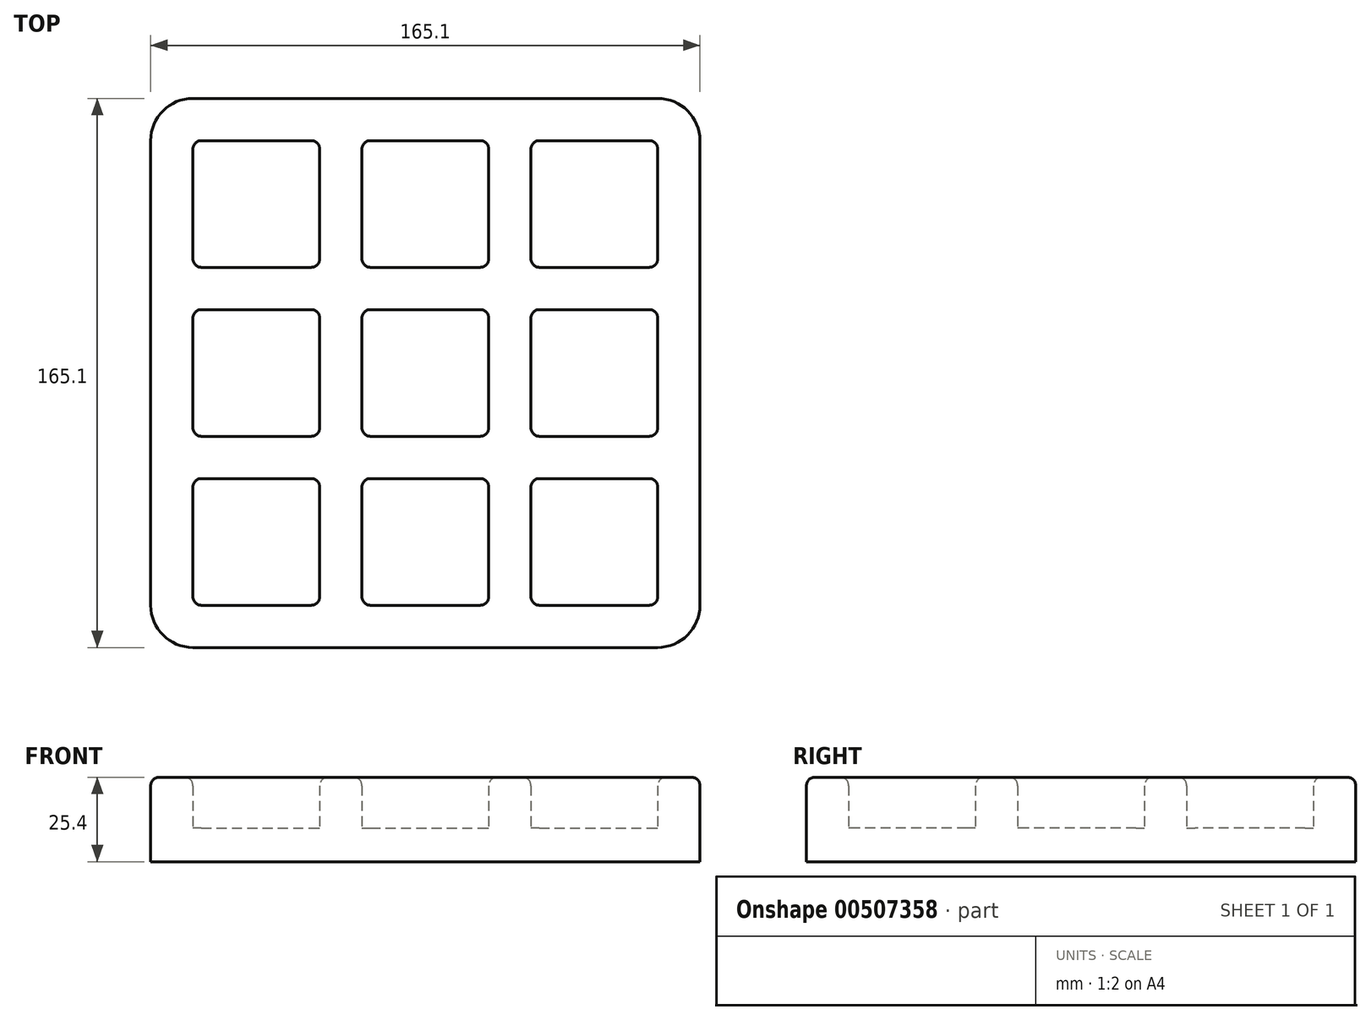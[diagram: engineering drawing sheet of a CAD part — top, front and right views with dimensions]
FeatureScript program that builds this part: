
annotation { "Feature Type Name" : "Feature", "Feature Type Description" : "" }
export const myFeature = defineFeature(function(context is Context, id is Id, definition is map)
    precondition{}
    {
        {
            var Q0;
            Q0=qCreatedBy(makeId("Top.planeOp"),FACE);
            var sketch = newSketch(context, id + "F0", { "sketchPlane" : qUnion([Q0])});
            skPoint(sketch, "E0.middle", {"position": v(0, 0) * mm});
            skLineSegment(sketch, "E1.bottom", {"start": v(-69.85, 69.85) * mm, "end": v(-31.75, 69.85) * mm});
            skLineSegment(sketch, "E1.top", {"start": v(-69.85, 31.75) * mm, "end": v(-31.75, 31.75) * mm});
            skLineSegment(sketch, "E1.left", {"start": v(-69.85, 69.85) * mm, "end": v(-69.85, 31.75) * mm});
            skLineSegment(sketch, "E1.right", {"start": v(-31.75, 69.85) * mm, "end": v(-31.75, 31.75) * mm});
            skPoint(sketch, "E1.middle", {"position": v(-50.8, 50.8) * mm});
            skPoint(sketch, "E2.0.1.0", {"position": v(-50.8, 0) * mm});
            skLineSegment(sketch, "E2.0.1.1", {"start": v(-69.85, 19.05) * mm, "end": v(-31.75, 19.05) * mm});
            skLineSegment(sketch, "E2.0.1.2", {"start": v(-31.75, 19.05) * mm, "end": v(-31.75, -19.05) * mm});
            skLineSegment(sketch, "E2.0.1.3", {"start": v(-69.85, -19.05) * mm, "end": v(-31.75, -19.05) * mm});
            skLineSegment(sketch, "E2.0.1.4", {"start": v(-69.85, 19.05) * mm, "end": v(-69.85, -19.05) * mm});
            skPoint(sketch, "E2.0.2.0", {"position": v(-50.8, -50.8) * mm});
            skLineSegment(sketch, "E2.0.2.1", {"start": v(-69.85, -31.75) * mm, "end": v(-31.75, -31.75) * mm});
            skLineSegment(sketch, "E2.0.2.2", {"start": v(-31.75, -31.75) * mm, "end": v(-31.75, -69.85) * mm});
            skLineSegment(sketch, "E2.0.2.3", {"start": v(-69.85, -69.85) * mm, "end": v(-31.75, -69.85) * mm});
            skLineSegment(sketch, "E2.0.2.4", {"start": v(-69.85, -31.75) * mm, "end": v(-69.85, -69.85) * mm});
            skPoint(sketch, "E2.1.0.0", {"position": v(0, 50.8) * mm});
            skLineSegment(sketch, "E2.1.0.1", {"start": v(-19.05, 69.85) * mm, "end": v(19.05, 69.85) * mm});
            skLineSegment(sketch, "E2.1.0.2", {"start": v(19.05, 69.85) * mm, "end": v(19.05, 31.75) * mm});
            skLineSegment(sketch, "E2.1.0.3", {"start": v(-19.05, 31.75) * mm, "end": v(19.05, 31.75) * mm});
            skLineSegment(sketch, "E2.1.0.4", {"start": v(-19.05, 69.85) * mm, "end": v(-19.05, 31.75) * mm});
            skLineSegment(sketch, "E2.1.1.1", {"start": v(-19.05, 19.05) * mm, "end": v(19.05, 19.05) * mm});
            skLineSegment(sketch, "E2.1.1.2", {"start": v(19.05, 19.05) * mm, "end": v(19.05, -19.05) * mm});
            skLineSegment(sketch, "E2.1.1.3", {"start": v(-19.05, -19.05) * mm, "end": v(19.05, -19.05) * mm});
            skLineSegment(sketch, "E2.1.1.4", {"start": v(-19.05, 19.05) * mm, "end": v(-19.05, -19.05) * mm});
            skPoint(sketch, "E2.1.2.0", {"position": v(0, -50.8) * mm});
            skLineSegment(sketch, "E2.1.2.1", {"start": v(-19.05, -31.75) * mm, "end": v(19.05, -31.75) * mm});
            skLineSegment(sketch, "E2.1.2.2", {"start": v(19.05, -31.75) * mm, "end": v(19.05, -69.85) * mm});
            skLineSegment(sketch, "E2.1.2.3", {"start": v(-19.05, -69.85) * mm, "end": v(19.05, -69.85) * mm});
            skLineSegment(sketch, "E2.1.2.4", {"start": v(-19.05, -31.75) * mm, "end": v(-19.05, -69.85) * mm});
            skPoint(sketch, "E2.2.0.0", {"position": v(50.8, 50.8) * mm});
            skLineSegment(sketch, "E2.2.0.1", {"start": v(31.75, 69.85) * mm, "end": v(69.85, 69.85) * mm});
            skLineSegment(sketch, "E2.2.0.2", {"start": v(69.85, 69.85) * mm, "end": v(69.85, 31.75) * mm});
            skLineSegment(sketch, "E2.2.0.3", {"start": v(31.75, 31.75) * mm, "end": v(69.85, 31.75) * mm});
            skLineSegment(sketch, "E2.2.0.4", {"start": v(31.75, 69.85) * mm, "end": v(31.75, 31.75) * mm});
            skPoint(sketch, "E2.2.1.0", {"position": v(50.8, 0) * mm});
            skLineSegment(sketch, "E2.2.1.1", {"start": v(31.75, 19.05) * mm, "end": v(69.85, 19.05) * mm});
            skLineSegment(sketch, "E2.2.1.2", {"start": v(69.85, 19.05) * mm, "end": v(69.85, -19.05) * mm});
            skLineSegment(sketch, "E2.2.1.3", {"start": v(31.75, -19.05) * mm, "end": v(69.85, -19.05) * mm});
            skLineSegment(sketch, "E2.2.1.4", {"start": v(31.75, 19.05) * mm, "end": v(31.75, -19.05) * mm});
            skPoint(sketch, "E2.2.2.0", {"position": v(50.8, -50.8) * mm});
            skLineSegment(sketch, "E2.2.2.1", {"start": v(31.75, -31.75) * mm, "end": v(69.85, -31.75) * mm});
            skLineSegment(sketch, "E2.2.2.2", {"start": v(69.85, -31.75) * mm, "end": v(69.85, -69.85) * mm});
            skLineSegment(sketch, "E2.2.2.3", {"start": v(31.75, -69.85) * mm, "end": v(69.85, -69.85) * mm});
            skLineSegment(sketch, "E2.2.2.4", {"start": v(31.75, -31.75) * mm, "end": v(31.75, -69.85) * mm});
            skLineSegment(sketch, "E2.direction1", {"start": v(-50.8, 50.8) * mm, "end": v(0, 50.8) * mm, "construction": true});
            skLineSegment(sketch, "E2.direction2", {"start": v(-50.8, 50.8) * mm, "end": v(-50.8, 0) * mm, "construction": true});
            skLineSegment(sketch, "E3.bottom", {"start": v(-82.55, 82.55) * mm, "end": v(82.55, 82.55) * mm});
            skLineSegment(sketch, "E3.top", {"start": v(-82.55, -82.55) * mm, "end": v(82.55, -82.55) * mm});
            skLineSegment(sketch, "E3.left", {"start": v(-82.55, 82.55) * mm, "end": v(-82.55, -82.55) * mm});
            skLineSegment(sketch, "E3.right", {"start": v(82.55, 82.55) * mm, "end": v(82.55, -82.55) * mm});
            skSolve(sketch);
        }
        {
            var Q0;
            Q0=makeQuery(id+"F0.imprint","IMPRINT",FACE,{"disambiguationData":[TD([[makeQuery(id+"F0.imprint","IMPRINT",EDGE,{"derivedFrom":sQuery(id+"F0.wireOp",EDGE,"E1.bottom")}),1.0]])]});
            extrude(context, id + "F1", {"entities" : qUnion([Q0]), "depth" : 25.4 * mm});
        }
        {
            var Q0;
            Q0=makeQuery(id+"F0.imprint","IMPRINT",FACE,{"disambiguationData":[TD([[makeQuery(id+"F0.imprint","IMPRINT",EDGE,{"derivedFrom":sQuery(id+"F0.wireOp",EDGE,"E1.bottom")}),-1.0]])]});
            var Q1;
            Q1=makeQuery(id+"F0.imprint","IMPRINT",FACE,{"disambiguationData":[TD([[makeQuery(id+"F0.imprint","IMPRINT",EDGE,{"derivedFrom":sQuery(id+"F0.wireOp",EDGE,"E2.1.0.1")}),-1.0]])]});
            var Q2;
            Q2=makeQuery(id+"F0.imprint","IMPRINT",FACE,{"disambiguationData":[TD([[makeQuery(id+"F0.imprint","IMPRINT",EDGE,{"derivedFrom":sQuery(id+"F0.wireOp",EDGE,"E2.2.0.1")}),-1.0]])]});
            var Q3;
            Q3=makeQuery(id+"F0.imprint","IMPRINT",FACE,{"disambiguationData":[TD([[makeQuery(id+"F0.imprint","IMPRINT",EDGE,{"derivedFrom":sQuery(id+"F0.wireOp",EDGE,"E2.2.1.1")}),-1.0]])]});
            var Q4;
            Q4=makeQuery(id+"F0.imprint","IMPRINT",FACE,{"disambiguationData":[TD([[makeQuery(id+"F0.imprint","IMPRINT",EDGE,{"derivedFrom":sQuery(id+"F0.wireOp",EDGE,"E2.2.2.1")}),-1.0]])]});
            var Q5;
            Q5=makeQuery(id+"F0.imprint","IMPRINT",FACE,{"disambiguationData":[TD([[makeQuery(id+"F0.imprint","IMPRINT",EDGE,{"derivedFrom":sQuery(id+"F0.wireOp",EDGE,"E2.1.1.1")}),-1.0]])]});
            var Q6;
            Q6=makeQuery(id+"F0.imprint","IMPRINT",FACE,{"disambiguationData":[TD([[makeQuery(id+"F0.imprint","IMPRINT",EDGE,{"derivedFrom":sQuery(id+"F0.wireOp",EDGE,"E2.1.2.1")}),-1.0]])]});
            var Q7;
            Q7=makeQuery(id+"F0.imprint","IMPRINT",FACE,{"disambiguationData":[TD([[makeQuery(id+"F0.imprint","IMPRINT",EDGE,{"derivedFrom":sQuery(id+"F0.wireOp",EDGE,"E2.0.2.1")}),-1.0]])]});
            var Q8;
            Q8=makeQuery(id+"F0.imprint","IMPRINT",FACE,{"disambiguationData":[TD([[makeQuery(id+"F0.imprint","IMPRINT",EDGE,{"derivedFrom":sQuery(id+"F0.wireOp",EDGE,"E2.0.1.1")}),-1.0]])]});
            extrude(context, id + "F2", {"entities" : qUnion([Q0, Q1, Q2, Q3, Q4, Q5, Q6, Q7, Q8]), "operationType" : NewBodyOperationType.ADD, "depth" : 10.16 * mm});
        }
        {
            var Q0;
            Q0=makeQuery(id+"F1.opExtrude","CAP_EDGE",EDGE,{"disambiguationData":[OSD([sQuery(id+"F0.wireOp",EDGE,"E3.right")])],"isStart":false});
            var Q1;
            Q1=makeQuery(id+"F2.opExtrude","CAP_EDGE",EDGE,{"disambiguationData":[OSD([sQuery(id+"F0.wireOp",EDGE,"E2.2.1.2")])],"isStart":false});
            var Q2;
            Q2=makeQuery(id+"F2.opExtrude","CAP_EDGE",EDGE,{"disambiguationData":[OSD([sQuery(id+"F0.wireOp",EDGE,"E2.2.0.2")])],"isStart":false});
            var Q3;
            Q3=makeQuery(id+"F1.opExtrude","CAP_EDGE",EDGE,{"disambiguationData":[OSD([sQuery(id+"F0.wireOp",EDGE,"E3.left")])],"isStart":false});
            var Q4;
            Q4=makeQuery(id+"F1.opExtrude","CAP_EDGE",EDGE,{"disambiguationData":[OSD([sQuery(id+"F0.wireOp",EDGE,"E2.2.2.3")])],"isStart":false});
            var Q5;
            Q5=makeQuery(id+"F1.opExtrude","CAP_EDGE",EDGE,{"disambiguationData":[OSD([sQuery(id+"F0.wireOp",EDGE,"E3.top")])],"isStart":false});
            var Q6;
            Q6=makeQuery(id+"F2.opExtrude","CAP_EDGE",EDGE,{"disambiguationData":[OSD([sQuery(id+"F0.wireOp",EDGE,"E2.0.2.2")])],"isStart":false});
            var Q7;
            Q7=makeQuery(id+"F2.opExtrude","CAP_EDGE",EDGE,{"disambiguationData":[OSD([sQuery(id+"F0.wireOp",EDGE,"E1.right")])],"isStart":false});
            var Q8;
            Q8=makeQuery(id+"F1.opExtrude","CAP_EDGE",EDGE,{"disambiguationData":[OSD([sQuery(id+"F0.wireOp",EDGE,"E1.bottom")])],"isStart":false});
            var Q9;
            Q9=makeQuery(id+"F1.opExtrude","CAP_EDGE",EDGE,{"disambiguationData":[OSD([sQuery(id+"F0.wireOp",EDGE,"E2.1.0.1")])],"isStart":false});
            var Q10;
            Q10=makeQuery(id+"F1.opExtrude","CAP_EDGE",EDGE,{"disambiguationData":[OSD([sQuery(id+"F0.wireOp",EDGE,"E2.0.2.1")])],"isStart":false});
            var Q11;
            Q11=makeQuery(id+"F1.opExtrude","CAP_EDGE",EDGE,{"disambiguationData":[OSD([sQuery(id+"F0.wireOp",EDGE,"E2.2.1.2")])],"isStart":false});
            var Q12;
            Q12=makeQuery(id+"F2.opExtrude","CAP_EDGE",EDGE,{"disambiguationData":[OSD([sQuery(id+"F0.wireOp",EDGE,"E1.bottom")])],"isStart":false});
            var Q13;
            Q13=makeQuery(id+"F2.opExtrude","CAP_EDGE",EDGE,{"disambiguationData":[OSD([sQuery(id+"F0.wireOp",EDGE,"E2.0.2.1")])],"isStart":false});
            var Q14;
            Q14=makeQuery(id+"F1.opExtrude","CAP_EDGE",EDGE,{"disambiguationData":[OSD([sQuery(id+"F0.wireOp",EDGE,"E2.1.2.1")])],"isStart":false});
            var Q15;
            Q15=makeQuery(id+"F2.opExtrude","CAP_EDGE",EDGE,{"disambiguationData":[OSD([sQuery(id+"F0.wireOp",EDGE,"E2.2.2.2")])],"isStart":false});
            var Q16;
            Q16=makeQuery(id+"F1.opExtrude","CAP_EDGE",EDGE,{"disambiguationData":[OSD([sQuery(id+"F0.wireOp",EDGE,"E2.2.2.1")])],"isStart":false});
            var Q17;
            Q17=makeQuery(id+"F1.opExtrude","CAP_EDGE",EDGE,{"disambiguationData":[OSD([sQuery(id+"F0.wireOp",EDGE,"E1.right")])],"isStart":false});
            var Q18;
            Q18=makeQuery(id+"F1.opExtrude","CAP_EDGE",EDGE,{"disambiguationData":[OSD([sQuery(id+"F0.wireOp",EDGE,"E2.2.2.2")])],"isStart":false});
            var Q19;
            Q19=makeQuery(id+"F1.opExtrude","CAP_EDGE",EDGE,{"disambiguationData":[OSD([sQuery(id+"F0.wireOp",EDGE,"E2.2.0.1")])],"isStart":false});
            var Q20;
            Q20=makeQuery(id+"F1.opExtrude","CAP_EDGE",EDGE,{"disambiguationData":[OSD([sQuery(id+"F0.wireOp",EDGE,"E3.bottom")])],"isStart":false});
            var Q21;
            Q21=makeQuery(id+"F1.opExtrude","CAP_EDGE",EDGE,{"disambiguationData":[OSD([sQuery(id+"F0.wireOp",EDGE,"E2.0.2.2")])],"isStart":false});
            var Q22;
            Q22=makeQuery(id+"F1.opExtrude","CAP_EDGE",EDGE,{"disambiguationData":[OSD([sQuery(id+"F0.wireOp",EDGE,"E2.2.0.2")])],"isStart":false});
            var Q23;
            Q23=makeQuery(id+"F2.opExtrude","CAP_EDGE",EDGE,{"disambiguationData":[OSD([sQuery(id+"F0.wireOp",EDGE,"E2.2.0.1")])],"isStart":false});
            var Q24;
            Q24=makeQuery(id+"F1.opExtrude","CAP_EDGE",EDGE,{"disambiguationData":[OSD([sQuery(id+"F0.wireOp",EDGE,"E2.1.1.2")])],"isStart":false});
            var Q25;
            Q25=makeQuery(id+"F2.opExtrude","CAP_EDGE",EDGE,{"disambiguationData":[OSD([sQuery(id+"F0.wireOp",EDGE,"E1.top")])],"isStart":false});
            var Q26;
            Q26=makeQuery(id+"F2.opExtrude","CAP_EDGE",EDGE,{"disambiguationData":[OSD([sQuery(id+"F0.wireOp",EDGE,"E2.1.1.2")])],"isStart":false});
            var Q27;
            Q27=makeQuery(id+"F1.opExtrude","SWEPT_EDGE",EDGE,{"disambiguationData":[OSD([sQuery(id+"F0.wireOp",EDGE,"E1.bottom"),sQuery(id+"F0.wireOp",EDGE,"E1.left")])]});
            var Q28;
            Q28=makeQuery(id+"F2.opExtrude","CAP_EDGE",EDGE,{"disambiguationData":[OSD([sQuery(id+"F0.wireOp",EDGE,"E2.1.2.2")])],"isStart":false});
            var Q29;
            Q29=makeQuery(id+"F1.opExtrude","CAP_EDGE",EDGE,{"disambiguationData":[OSD([sQuery(id+"F0.wireOp",EDGE,"E2.1.0.4")])],"isStart":false});
            var Q30;
            Q30=makeQuery(id+"F1.opExtrude","CAP_EDGE",EDGE,{"disambiguationData":[OSD([sQuery(id+"F0.wireOp",EDGE,"E2.0.1.4")])],"isStart":false});
            var Q31;
            Q31=makeQuery(id+"F2.opExtrude","CAP_EDGE",EDGE,{"disambiguationData":[OSD([sQuery(id+"F0.wireOp",EDGE,"E2.0.1.1")])],"isStart":false});
            var Q32;
            Q32=makeQuery(id+"F1.opExtrude","SWEPT_EDGE",EDGE,{"disambiguationData":[OSD([sQuery(id+"F0.wireOp",EDGE,"E2.0.2.3"),sQuery(id+"F0.wireOp",EDGE,"E2.0.2.4")])]});
            var Q33;
            Q33=makeQuery(id+"F1.opExtrude","SWEPT_EDGE",EDGE,{"disambiguationData":[OSD([sQuery(id+"F0.wireOp",EDGE,"E2.2.2.1"),sQuery(id+"F0.wireOp",EDGE,"E2.2.2.2")])]});
            var Q34;
            Q34=makeQuery(id+"F1.opExtrude","SWEPT_EDGE",EDGE,{"disambiguationData":[OSD([sQuery(id+"F0.wireOp",EDGE,"E2.0.2.2"),sQuery(id+"F0.wireOp",EDGE,"E2.0.2.3")])]});
            var Q35;
            Q35=makeQuery(id+"F1.opExtrude","CAP_EDGE",EDGE,{"disambiguationData":[OSD([sQuery(id+"F0.wireOp",EDGE,"E2.0.1.3")])],"isStart":false});
            var Q36;
            Q36=makeQuery(id+"F1.opExtrude","CAP_EDGE",EDGE,{"disambiguationData":[OSD([sQuery(id+"F0.wireOp",EDGE,"E2.0.1.2")])],"isStart":false});
            var Q37;
            Q37=makeQuery(id+"F1.opExtrude","CAP_EDGE",EDGE,{"disambiguationData":[OSD([sQuery(id+"F0.wireOp",EDGE,"E2.0.1.1")])],"isStart":false});
            var Q38;
            Q38=makeQuery(id+"F1.opExtrude","CAP_EDGE",EDGE,{"disambiguationData":[OSD([sQuery(id+"F0.wireOp",EDGE,"E2.2.1.1")])],"isStart":false});
            var Q39;
            Q39=makeQuery(id+"F1.opExtrude","SWEPT_EDGE",EDGE,{"disambiguationData":[OSD([sQuery(id+"F0.wireOp",EDGE,"E1.bottom"),sQuery(id+"F0.wireOp",EDGE,"E1.right")])]});
            var Q40;
            Q40=makeQuery(id+"F1.opExtrude","SWEPT_EDGE",EDGE,{"disambiguationData":[OSD([sQuery(id+"F0.wireOp",EDGE,"E2.0.1.3"),sQuery(id+"F0.wireOp",EDGE,"E2.0.1.4")])]});
            var Q41;
            Q41=makeQuery(id+"F2.opExtrude","CAP_EDGE",EDGE,{"disambiguationData":[OSD([sQuery(id+"F0.wireOp",EDGE,"E2.0.2.3")])],"isStart":false});
            var Q42;
            Q42=makeQuery(id+"F2.opExtrude","CAP_EDGE",EDGE,{"disambiguationData":[OSD([sQuery(id+"F0.wireOp",EDGE,"E2.0.1.2")])],"isStart":false});
            var Q43;
            Q43=makeQuery(id+"F1.opExtrude","CAP_EDGE",EDGE,{"disambiguationData":[OSD([sQuery(id+"F0.wireOp",EDGE,"E2.1.2.4")])],"isStart":false});
            var Q44;
            Q44=makeQuery(id+"F1.opExtrude","CAP_EDGE",EDGE,{"disambiguationData":[OSD([sQuery(id+"F0.wireOp",EDGE,"E2.0.2.4")])],"isStart":false});
            var Q45;
            Q45=makeQuery(id+"F2.opExtrude","CAP_EDGE",EDGE,{"disambiguationData":[OSD([sQuery(id+"F0.wireOp",EDGE,"E2.1.2.1")])],"isStart":false});
            var Q46;
            Q46=makeQuery(id+"F2.opExtrude","CAP_EDGE",EDGE,{"disambiguationData":[OSD([sQuery(id+"F0.wireOp",EDGE,"E2.2.2.1")])],"isStart":false});
            var Q47;
            Q47=makeQuery(id+"F1.opExtrude","SWEPT_EDGE",EDGE,{"disambiguationData":[OSD([sQuery(id+"F0.wireOp",EDGE,"E2.2.0.1"),sQuery(id+"F0.wireOp",EDGE,"E2.2.0.2")])]});
            var Q48;
            Q48=makeQuery(id+"F1.opExtrude","SWEPT_EDGE",EDGE,{"disambiguationData":[OSD([sQuery(id+"F0.wireOp",EDGE,"E2.2.2.2"),sQuery(id+"F0.wireOp",EDGE,"E2.2.2.3")])]});
            var Q49;
            Q49=makeQuery(id+"F2.opExtrude","CAP_EDGE",EDGE,{"disambiguationData":[OSD([sQuery(id+"F0.wireOp",EDGE,"E2.1.2.4")])],"isStart":false});
            var Q50;
            Q50=makeQuery(id+"F1.opExtrude","SWEPT_EDGE",EDGE,{"disambiguationData":[OSD([sQuery(id+"F0.wireOp",EDGE,"E2.1.2.1"),sQuery(id+"F0.wireOp",EDGE,"E2.1.2.2")])]});
            var Q51;
            Q51=makeQuery(id+"F2.opExtrude","CAP_EDGE",EDGE,{"disambiguationData":[OSD([sQuery(id+"F0.wireOp",EDGE,"E2.0.1.4")])],"isStart":false});
            var Q52;
            Q52=makeQuery(id+"F1.opExtrude","CAP_EDGE",EDGE,{"disambiguationData":[OSD([sQuery(id+"F0.wireOp",EDGE,"E2.2.1.3")])],"isStart":false});
            var Q53;
            Q53=makeQuery(id+"F1.opExtrude","CAP_EDGE",EDGE,{"disambiguationData":[OSD([sQuery(id+"F0.wireOp",EDGE,"E2.1.2.3")])],"isStart":false});
            var Q54;
            Q54=makeQuery(id+"F1.opExtrude","SWEPT_EDGE",EDGE,{"disambiguationData":[OSD([sQuery(id+"F0.wireOp",EDGE,"E2.1.0.1"),sQuery(id+"F0.wireOp",EDGE,"E2.1.0.4")])]});
            var Q55;
            Q55=makeQuery(id+"F1.opExtrude","CAP_EDGE",EDGE,{"disambiguationData":[OSD([sQuery(id+"F0.wireOp",EDGE,"E2.1.1.3")])],"isStart":false});
            var Q56;
            Q56=makeQuery(id+"F2.opExtrude","CAP_EDGE",EDGE,{"disambiguationData":[OSD([sQuery(id+"F0.wireOp",EDGE,"E2.2.1.1")])],"isStart":false});
            var Q57;
            Q57=makeQuery(id+"F1.opExtrude","SWEPT_EDGE",EDGE,{"disambiguationData":[OSD([sQuery(id+"F0.wireOp",EDGE,"E2.2.1.2"),sQuery(id+"F0.wireOp",EDGE,"E2.2.1.3")])]});
            var Q58;
            Q58=makeQuery(id+"F1.opExtrude","CAP_EDGE",EDGE,{"disambiguationData":[OSD([sQuery(id+"F0.wireOp",EDGE,"E1.left")])],"isStart":false});
            var Q59;
            Q59=makeQuery(id+"F1.opExtrude","SWEPT_EDGE",EDGE,{"disambiguationData":[OSD([sQuery(id+"F0.wireOp",EDGE,"E2.0.2.1"),sQuery(id+"F0.wireOp",EDGE,"E2.0.2.2")])]});
            var Q60;
            Q60=makeQuery(id+"F1.opExtrude","SWEPT_EDGE",EDGE,{"disambiguationData":[OSD([sQuery(id+"F0.wireOp",EDGE,"E2.1.2.3"),sQuery(id+"F0.wireOp",EDGE,"E2.1.2.4")])]});
            var Q61;
            Q61=makeQuery(id+"F1.opExtrude","CAP_EDGE",EDGE,{"disambiguationData":[OSD([sQuery(id+"F0.wireOp",EDGE,"E2.1.2.2")])],"isStart":false});
            var Q62;
            Q62=makeQuery(id+"F1.opExtrude","SWEPT_EDGE",EDGE,{"disambiguationData":[OSD([sQuery(id+"F0.wireOp",EDGE,"E1.top"),sQuery(id+"F0.wireOp",EDGE,"E1.left")])]});
            var Q63;
            Q63=makeQuery(id+"F1.opExtrude","CAP_EDGE",EDGE,{"disambiguationData":[OSD([sQuery(id+"F0.wireOp",EDGE,"E1.top")])],"isStart":false});
            var Q64;
            Q64=makeQuery(id+"F1.opExtrude","CAP_EDGE",EDGE,{"disambiguationData":[OSD([sQuery(id+"F0.wireOp",EDGE,"E2.1.0.2")])],"isStart":false});
            var Q65;
            Q65=makeQuery(id+"F2.opExtrude","CAP_EDGE",EDGE,{"disambiguationData":[OSD([sQuery(id+"F0.wireOp",EDGE,"E2.1.0.1")])],"isStart":false});
            var Q66;
            Q66=makeQuery(id+"F2.opExtrude","CAP_EDGE",EDGE,{"disambiguationData":[OSD([sQuery(id+"F0.wireOp",EDGE,"E2.1.0.3")])],"isStart":false});
            var Q67;
            Q67=makeQuery(id+"F1.opExtrude","SWEPT_EDGE",EDGE,{"disambiguationData":[OSD([sQuery(id+"F0.wireOp",EDGE,"E2.0.2.1"),sQuery(id+"F0.wireOp",EDGE,"E2.0.2.4")])]});
            var Q68;
            Q68=makeQuery(id+"F2.opExtrude","CAP_EDGE",EDGE,{"disambiguationData":[OSD([sQuery(id+"F0.wireOp",EDGE,"E2.1.2.3")])],"isStart":false});
            var Q69;
            Q69=makeQuery(id+"F1.opExtrude","CAP_EDGE",EDGE,{"disambiguationData":[OSD([sQuery(id+"F0.wireOp",EDGE,"E2.1.1.1")])],"isStart":false});
            var Q70;
            Q70=makeQuery(id+"F2.opExtrude","CAP_EDGE",EDGE,{"disambiguationData":[OSD([sQuery(id+"F0.wireOp",EDGE,"E2.0.2.4")])],"isStart":false});
            var Q71;
            Q71=makeQuery(id+"F2.opExtrude","CAP_EDGE",EDGE,{"disambiguationData":[OSD([sQuery(id+"F0.wireOp",EDGE,"E1.left")])],"isStart":false});
            var Q72;
            Q72=makeQuery(id+"F2.opExtrude","CAP_EDGE",EDGE,{"disambiguationData":[OSD([sQuery(id+"F0.wireOp",EDGE,"E2.1.0.2")])],"isStart":false});
            var Q73;
            Q73=makeQuery(id+"F1.opExtrude","SWEPT_EDGE",EDGE,{"disambiguationData":[OSD([sQuery(id+"F0.wireOp",EDGE,"E2.1.2.2"),sQuery(id+"F0.wireOp",EDGE,"E2.1.2.3")])]});
            var Q74;
            Q74=makeQuery(id+"F2.opExtrude","CAP_EDGE",EDGE,{"disambiguationData":[OSD([sQuery(id+"F0.wireOp",EDGE,"E2.2.1.3")])],"isStart":false});
            var Q75;
            Q75=makeQuery(id+"F2.opExtrude","CAP_EDGE",EDGE,{"disambiguationData":[OSD([sQuery(id+"F0.wireOp",EDGE,"E2.1.0.4")])],"isStart":false});
            var Q76;
            Q76=makeQuery(id+"F1.opExtrude","CAP_EDGE",EDGE,{"disambiguationData":[OSD([sQuery(id+"F0.wireOp",EDGE,"E2.0.2.3")])],"isStart":false});
            var Q77;
            Q77=makeQuery(id+"F1.opExtrude","SWEPT_EDGE",EDGE,{"disambiguationData":[OSD([sQuery(id+"F0.wireOp",EDGE,"E2.2.2.3"),sQuery(id+"F0.wireOp",EDGE,"E2.2.2.4")])]});
            var Q78;
            Q78=makeQuery(id+"F1.opExtrude","SWEPT_EDGE",EDGE,{"disambiguationData":[OSD([sQuery(id+"F0.wireOp",EDGE,"E1.top"),sQuery(id+"F0.wireOp",EDGE,"E1.right")])]});
            var Q79;
            Q79=makeQuery(id+"F1.opExtrude","CAP_EDGE",EDGE,{"disambiguationData":[OSD([sQuery(id+"F0.wireOp",EDGE,"E2.2.1.4")])],"isStart":false});
            var Q80;
            Q80=makeQuery(id+"F2.opExtrude","CAP_EDGE",EDGE,{"disambiguationData":[OSD([sQuery(id+"F0.wireOp",EDGE,"E2.2.2.4")])],"isStart":false});
            var Q81;
            Q81=makeQuery(id+"F1.opExtrude","SWEPT_EDGE",EDGE,{"disambiguationData":[OSD([sQuery(id+"F0.wireOp",EDGE,"E2.0.1.1"),sQuery(id+"F0.wireOp",EDGE,"E2.0.1.4")])]});
            var Q82;
            Q82=makeQuery(id+"F1.opExtrude","CAP_EDGE",EDGE,{"disambiguationData":[OSD([sQuery(id+"F0.wireOp",EDGE,"E2.2.0.3")])],"isStart":false});
            var Q83;
            Q83=makeQuery(id+"F1.opExtrude","SWEPT_EDGE",EDGE,{"disambiguationData":[OSD([sQuery(id+"F0.wireOp",EDGE,"E2.1.1.1"),sQuery(id+"F0.wireOp",EDGE,"E2.1.1.2")])]});
            var Q84;
            Q84=makeQuery(id+"F2.opExtrude","CAP_EDGE",EDGE,{"disambiguationData":[OSD([sQuery(id+"F0.wireOp",EDGE,"E2.2.1.4")])],"isStart":false});
            var Q85;
            Q85=makeQuery(id+"F1.opExtrude","CAP_EDGE",EDGE,{"disambiguationData":[OSD([sQuery(id+"F0.wireOp",EDGE,"E2.2.0.4")])],"isStart":false});
            var Q86;
            Q86=makeQuery(id+"F2.opExtrude","CAP_EDGE",EDGE,{"disambiguationData":[OSD([sQuery(id+"F0.wireOp",EDGE,"E2.0.1.3")])],"isStart":false});
            var Q87;
            Q87=makeQuery(id+"F1.opExtrude","SWEPT_EDGE",EDGE,{"disambiguationData":[OSD([sQuery(id+"F0.wireOp",EDGE,"E2.2.1.1"),sQuery(id+"F0.wireOp",EDGE,"E2.2.1.2")])]});
            var Q88;
            Q88=makeQuery(id+"F1.opExtrude","SWEPT_EDGE",EDGE,{"disambiguationData":[OSD([sQuery(id+"F0.wireOp",EDGE,"E2.1.0.1"),sQuery(id+"F0.wireOp",EDGE,"E2.1.0.2")])]});
            var Q89;
            Q89=makeQuery(id+"F1.opExtrude","SWEPT_EDGE",EDGE,{"disambiguationData":[OSD([sQuery(id+"F0.wireOp",EDGE,"E2.1.1.3"),sQuery(id+"F0.wireOp",EDGE,"E2.1.1.4")])]});
            var Q90;
            Q90=makeQuery(id+"F2.opExtrude","CAP_EDGE",EDGE,{"disambiguationData":[OSD([sQuery(id+"F0.wireOp",EDGE,"E2.1.1.1")])],"isStart":false});
            var Q91;
            Q91=makeQuery(id+"F2.opExtrude","CAP_EDGE",EDGE,{"disambiguationData":[OSD([sQuery(id+"F0.wireOp",EDGE,"E2.2.2.3")])],"isStart":false});
            var Q92;
            Q92=makeQuery(id+"F1.opExtrude","SWEPT_EDGE",EDGE,{"disambiguationData":[OSD([sQuery(id+"F0.wireOp",EDGE,"E2.2.0.3"),sQuery(id+"F0.wireOp",EDGE,"E2.2.0.4")])]});
            var Q93;
            Q93=makeQuery(id+"F1.opExtrude","SWEPT_EDGE",EDGE,{"disambiguationData":[OSD([sQuery(id+"F0.wireOp",EDGE,"E2.2.0.1"),sQuery(id+"F0.wireOp",EDGE,"E2.2.0.4")])]});
            var Q94;
            Q94=makeQuery(id+"F2.opExtrude","CAP_EDGE",EDGE,{"disambiguationData":[OSD([sQuery(id+"F0.wireOp",EDGE,"E2.2.0.4")])],"isStart":false});
            var Q95;
            Q95=makeQuery(id+"F1.opExtrude","SWEPT_EDGE",EDGE,{"disambiguationData":[OSD([sQuery(id+"F0.wireOp",EDGE,"E2.0.1.2"),sQuery(id+"F0.wireOp",EDGE,"E2.0.1.3")])]});
            var Q96;
            Q96=makeQuery(id+"F1.opExtrude","CAP_EDGE",EDGE,{"disambiguationData":[OSD([sQuery(id+"F0.wireOp",EDGE,"E2.1.0.3")])],"isStart":false});
            var Q97;
            Q97=makeQuery(id+"F2.opExtrude","CAP_EDGE",EDGE,{"disambiguationData":[OSD([sQuery(id+"F0.wireOp",EDGE,"E2.1.1.3")])],"isStart":false});
            var Q98;
            Q98=makeQuery(id+"F1.opExtrude","SWEPT_EDGE",EDGE,{"disambiguationData":[OSD([sQuery(id+"F0.wireOp",EDGE,"E2.2.2.1"),sQuery(id+"F0.wireOp",EDGE,"E2.2.2.4")])]});
            var Q99;
            Q99=makeQuery(id+"F1.opExtrude","CAP_EDGE",EDGE,{"disambiguationData":[OSD([sQuery(id+"F0.wireOp",EDGE,"E2.1.1.4")])],"isStart":false});
            var Q100;
            Q100=makeQuery(id+"F1.opExtrude","SWEPT_EDGE",EDGE,{"disambiguationData":[OSD([sQuery(id+"F0.wireOp",EDGE,"E2.2.1.1"),sQuery(id+"F0.wireOp",EDGE,"E2.2.1.4")])]});
            var Q101;
            Q101=makeQuery(id+"F1.opExtrude","SWEPT_EDGE",EDGE,{"disambiguationData":[OSD([sQuery(id+"F0.wireOp",EDGE,"E2.1.0.2"),sQuery(id+"F0.wireOp",EDGE,"E2.1.0.3")])]});
            var Q102;
            Q102=makeQuery(id+"F2.opExtrude","CAP_EDGE",EDGE,{"disambiguationData":[OSD([sQuery(id+"F0.wireOp",EDGE,"E2.1.1.4")])],"isStart":false});
            var Q103;
            Q103=makeQuery(id+"F2.opExtrude","CAP_EDGE",EDGE,{"disambiguationData":[OSD([sQuery(id+"F0.wireOp",EDGE,"E2.2.0.3")])],"isStart":false});
            var Q104;
            Q104=makeQuery(id+"F1.opExtrude","SWEPT_EDGE",EDGE,{"disambiguationData":[OSD([sQuery(id+"F0.wireOp",EDGE,"E2.1.0.3"),sQuery(id+"F0.wireOp",EDGE,"E2.1.0.4")])]});
            var Q105;
            Q105=makeQuery(id+"F1.opExtrude","SWEPT_EDGE",EDGE,{"disambiguationData":[OSD([sQuery(id+"F0.wireOp",EDGE,"E2.1.1.2"),sQuery(id+"F0.wireOp",EDGE,"E2.1.1.3")])]});
            var Q106;
            Q106=makeQuery(id+"F1.opExtrude","SWEPT_EDGE",EDGE,{"disambiguationData":[OSD([sQuery(id+"F0.wireOp",EDGE,"E2.2.0.2"),sQuery(id+"F0.wireOp",EDGE,"E2.2.0.3")])]});
            var Q107;
            Q107=makeQuery(id+"F1.opExtrude","SWEPT_EDGE",EDGE,{"disambiguationData":[OSD([sQuery(id+"F0.wireOp",EDGE,"E2.1.1.1"),sQuery(id+"F0.wireOp",EDGE,"E2.1.1.4")])]});
            var Q108;
            Q108=makeQuery(id+"F1.opExtrude","SWEPT_EDGE",EDGE,{"disambiguationData":[OSD([sQuery(id+"F0.wireOp",EDGE,"E2.0.1.1"),sQuery(id+"F0.wireOp",EDGE,"E2.0.1.2")])]});
            var Q109;
            Q109=makeQuery(id+"F1.opExtrude","SWEPT_EDGE",EDGE,{"disambiguationData":[OSD([sQuery(id+"F0.wireOp",EDGE,"E2.2.1.3"),sQuery(id+"F0.wireOp",EDGE,"E2.2.1.4")])]});
            var Q110;
            Q110=makeQuery(id+"F1.opExtrude","SWEPT_EDGE",EDGE,{"disambiguationData":[OSD([sQuery(id+"F0.wireOp",EDGE,"E2.1.2.1"),sQuery(id+"F0.wireOp",EDGE,"E2.1.2.4")])]});
            var Q111;
            Q111=makeQuery(id+"F1.opExtrude","CAP_EDGE",EDGE,{"disambiguationData":[OSD([sQuery(id+"F0.wireOp",EDGE,"E2.2.2.4")])],"isStart":false});
            fillet(context, id + "F3", {"entities" : qUnion([Q0, Q1, Q2, Q3, Q4, Q5, Q6, Q7, Q8, Q9, Q10, Q11, Q12, Q13, Q14, Q15, Q16, Q17, Q18, Q19, Q20, Q21, Q22, Q23, Q24, Q25, Q26, Q27, Q28, Q29, Q30, Q31, Q32, Q33, Q34, Q35, Q36, Q37, Q38, Q39, Q40, Q41, Q42, Q43, Q44, Q45, Q46, Q47, Q48, Q49, Q50, Q51, Q52, Q53, Q54, Q55, Q56, Q57, Q58, Q59, Q60, Q61, Q62, Q63, Q64, Q65, Q66, Q67, Q68, Q69, Q70, Q71, Q72, Q73, Q74, Q75, Q76, Q77, Q78, Q79, Q80, Q81, Q82, Q83, Q84, Q85, Q86, Q87, Q88, Q89, Q90, Q91, Q92, Q93, Q94, Q95, Q96, Q97, Q98, Q99, Q100, Q101, Q102, Q103, Q104, Q105, Q106, Q107, Q108, Q109, Q110, Q111]), "radius" : 2.54 * mm, "tangentPropagation" : true, "allowEdgeOverflow" : false});
        }
        {
            var Q0;
            Q0=makeQuery(id+"F1.opExtrude","SWEPT_EDGE",EDGE,{"disambiguationData":[OSD([sQuery(id+"F0.wireOp",EDGE,"E3.bottom"),sQuery(id+"F0.wireOp",EDGE,"E3.right")])]});
            var Q1;
            Q1=makeQuery(id+"F1.opExtrude","SWEPT_EDGE",EDGE,{"disambiguationData":[OSD([sQuery(id+"F0.wireOp",EDGE,"E3.bottom"),sQuery(id+"F0.wireOp",EDGE,"E3.left")])]});
            var Q2;
            Q2=makeQuery(id+"F1.opExtrude","SWEPT_EDGE",EDGE,{"disambiguationData":[OSD([sQuery(id+"F0.wireOp",EDGE,"E3.top"),sQuery(id+"F0.wireOp",EDGE,"E3.right")])]});
            var Q3;
            Q3=makeQuery(id+"F1.opExtrude","SWEPT_EDGE",EDGE,{"disambiguationData":[OSD([sQuery(id+"F0.wireOp",EDGE,"E3.top"),sQuery(id+"F0.wireOp",EDGE,"E3.left")])]});
            fillet(context, id + "F4", {"entities" : qUnion([Q0, Q1, Q2, Q3]), "radius" : 12.7 * mm, "tangentPropagation" : true, "allowEdgeOverflow" : false});
        }
    });
